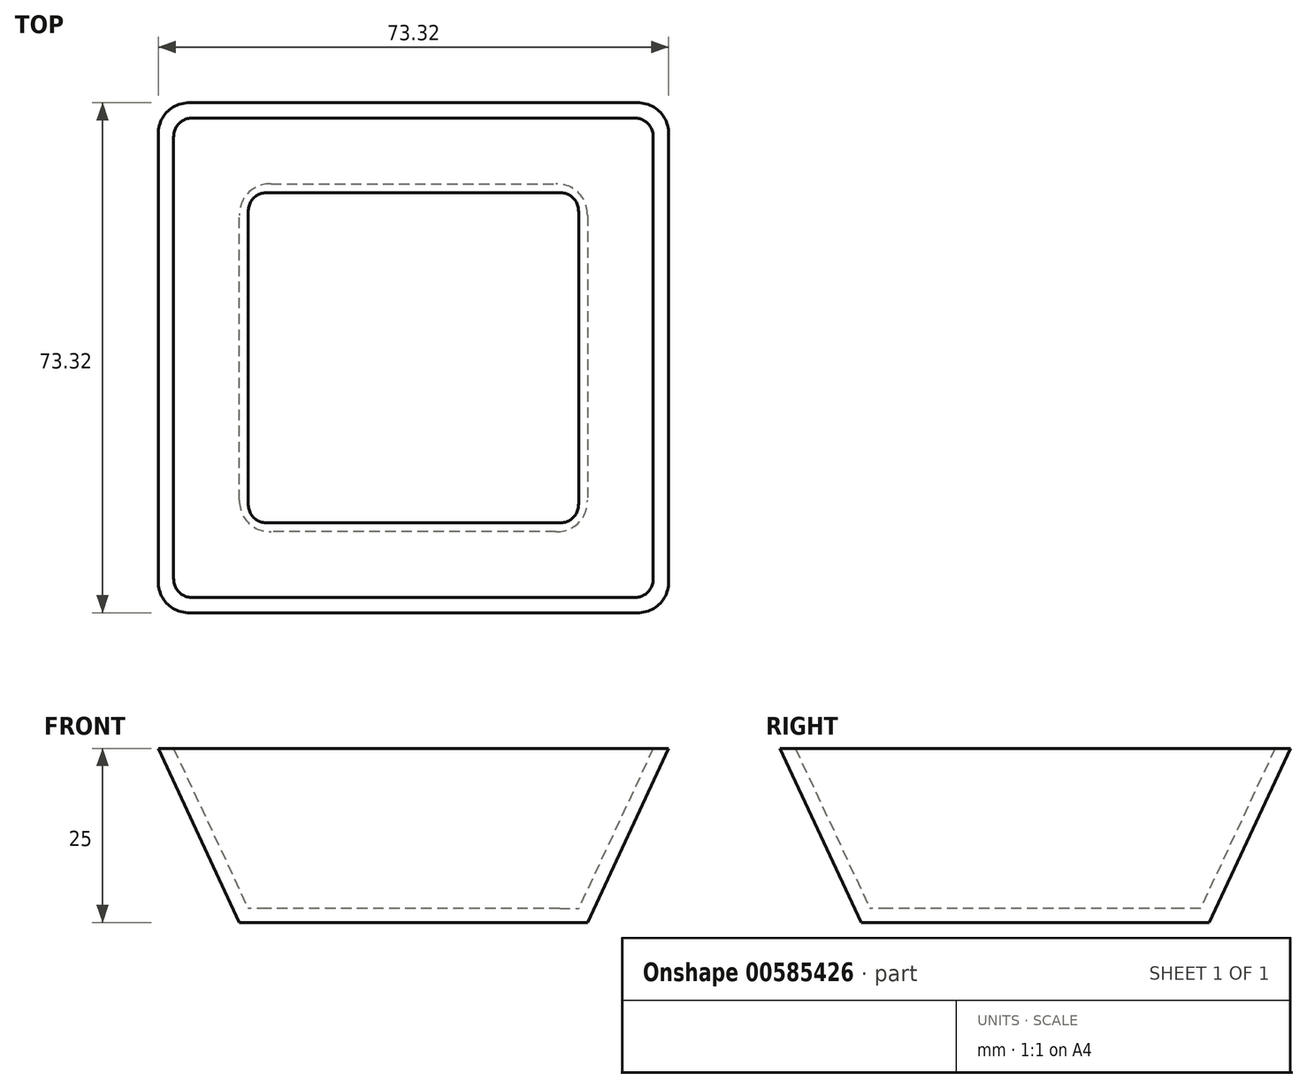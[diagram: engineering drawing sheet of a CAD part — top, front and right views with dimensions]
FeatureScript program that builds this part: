
annotation { "Feature Type Name" : "Feature", "Feature Type Description" : "" }
export const myFeature = defineFeature(function(context is Context, id is Id, definition is map)
    precondition{}
    {
        {
            var Q0;
            Q0=qCreatedBy(makeId("Top.planeOp"),FACE);
            var sketch = newSketch(context, id + "F0", { "sketchPlane" : qUnion([Q0])});
            skLineSegment(sketch, "E0.bottom", {"start": v(25, -25) * mm, "end": v(-25, -25) * mm});
            skLineSegment(sketch, "E0.top", {"start": v(25, 25) * mm, "end": v(-25, 25) * mm});
            skLineSegment(sketch, "E0.left", {"start": v(25, -25) * mm, "end": v(25, 25) * mm});
            skLineSegment(sketch, "E0.right", {"start": v(-25, -25) * mm, "end": v(-25, 25) * mm});
            skPoint(sketch, "E0.middle", {"position": v(0, 0) * mm});
            skSolve(sketch);
        }
        {
            var Q0;
            Q0=makeQuery(id+"F0.imprint","IMPRINT",FACE,{"disambiguationData":[TD([[makeQuery(id+"F0.imprint","IMPRINT",EDGE,{"derivedFrom":sQuery(id+"F0.wireOp",EDGE,"E0.bottom")}),-1.0]])]});
            extrude(context, id + "F1", {"entities" : qUnion([Q0]), "depth" : 25 * mm, "offsetDistance" : 25 * mm, "hasDraft" : true, "draftAngle" : 25 * degree});
        }
        {
            var Q0;
            Q0=makeQuery(id+"F1.opExtrude","SWEPT_EDGE",EDGE,{"disambiguationData":[OSD([sQuery(id+"F0.wireOp",EDGE,"E0.bottom"),sQuery(id+"F0.wireOp",EDGE,"E0.right")])]});
            var Q1;
            Q1=makeQuery(id+"F1.opExtrude","SWEPT_EDGE",EDGE,{"disambiguationData":[OSD([sQuery(id+"F0.wireOp",EDGE,"E0.top"),sQuery(id+"F0.wireOp",EDGE,"E0.right")])]});
            var Q2;
            Q2=makeQuery(id+"F1.opExtrude","SWEPT_EDGE",EDGE,{"disambiguationData":[OSD([sQuery(id+"F0.wireOp",EDGE,"E0.bottom"),sQuery(id+"F0.wireOp",EDGE,"E0.left")])]});
            var Q3;
            Q3=makeQuery(id+"F1.opExtrude","SWEPT_EDGE",EDGE,{"disambiguationData":[OSD([sQuery(id+"F0.wireOp",EDGE,"E0.top"),sQuery(id+"F0.wireOp",EDGE,"E0.left")])]});
            fillet(context, id + "F2", {"entities" : qUnion([Q0, Q1, Q2, Q3]), "radius" : 5 * mm, "tangentPropagation" : true, "allowEdgeOverflow" : false});
        }
        {
            var Q0;
            Q0=makeQuery(id+"F1.opExtrude","CAP_FACE",FACE,{"disambiguationData":[OSD([sQuery(id+"F0.wireOp",EDGE,"E0.bottom"),sQuery(id+"F0.wireOp",EDGE,"E0.top"),sQuery(id+"F0.wireOp",EDGE,"E0.left"),sQuery(id+"F0.wireOp",EDGE,"E0.right")])],"isStart":false});
            shell(context, id + "F3", {"entities" : qUnion([Q0]), "thickness" : 2 * mm});
        }
        {
            var Q0;
            Q0=makeQuery(id+"F3.opShell","OFFSET_FACE",FACE,{"disambiguationData":[OSD([sQuery(id+"F0.wireOp",EDGE,"E0.bottom"),sQuery(id+"F0.wireOp",EDGE,"E0.top"),sQuery(id+"F0.wireOp",EDGE,"E0.left"),sQuery(id+"F0.wireOp",EDGE,"E0.right")])]});
            var sketch = newSketch(context, id + "F4", { "sketchPlane" : qUnion([Q0])});
            skCircle(sketch, "E1", {"center": v(0, 0) * mm, "radius": 22 * mm});
            skSolve(sketch);
        }
        {
            var Q0;
            Q0=sQuery(id+"F4.wireOp",EDGE,"E1");
            extrude(context, id + "F5", {"bodyType" : ToolBodyType.SURFACE, "surfaceEntities" : qUnion([Q0]), "depth" : 1.5 * mm, "offsetDistance" : 25 * mm});
        }
    });
